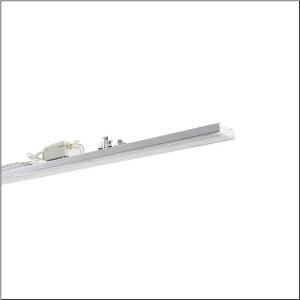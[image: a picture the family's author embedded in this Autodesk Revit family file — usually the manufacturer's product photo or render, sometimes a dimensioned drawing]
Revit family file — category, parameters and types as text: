
# Revit family: licross_11_recessed_mo_51tl107n485g
name_source: partatom
category: Lighting Fixtures
units: mm (PartAtom-declared; Revit-internal decimal feet)

## family parameters
Cut with Voids When Loaded = No
Host = Face
Light Source = No
Part Type = Normal
Room Calculation Point = No
Round Connector Dimension = Use Diameter
Shared = No

## types (1)
- Licross 11 Recessed MO (1 x LED, 8700 lm, 48.5 W, 4000K)
    Apparent Load = 49 VA
    CIE Flux Codes = 50 81 96 100 100
    Color Rendering = 80
    Color Temperature = 4000K
    Default Elevation = 1800 mm
    Description = Licross 11 Recessed MO, luminaire insert, of sheet steel, coil coated, white, length: 1.500mm, width: 66mm, height: 67mm, LED rated luminous flux: 8.710lm, light colour: 840, SDCM (Standard Deviation of Colour Matching)MacAdam ≤ 2 SDCM (initial), control gear: ON/OFF, with plug, 3-pole, with phase selection, mains connection: 220..240V, AC, 50/60Hz, rated input power: 49W, internal wiring halogen-free, primary optical cover: cover, of PMMA, light emission: direct distribution, primary light characteristic: symmetric, protection rating (complete): IP40, insulation class (complete): insulation class I (protective earthing), certification: CE, ENEC, VDE, UKCA, protection symbol: D if used in an environment without relevant dust loads with corresponding accessories, impact resistance: IK06, permissible ambient temperature for indoor applications: -35..+35°C, corresponds to IFS (International Featured Standards) requirements for safety and quality in the food industry, reducing of maximum allowable ambient temperature of 5°C with ceiling mounting, The light source and the operating device comply with the requirements of the Ecodesign Regulation (EU) 2019/2020 and are replaceable in accordance with this regulation, packaging unit: 1 piece
    Height = 58 mm
    Lamp = 1 x LED
    Lamp Light Flux = 8700 lm
    Lamp Power = 48.5 W
    Lamp count = 1
    Length = 1500 mm
    Luminous efficacy = 179 lm/W
    Manufacturer = Siteco
    ModVariant = No
    Model = 51TL107N485G
    Mounting Place = Ceiling
    Mounting Type = Pendant
    Number of Poles = 1
    OnlyDefault = Yes
    Power Factor = 1
    Product Name = Licross 11 Recessed MO
    Product group = luminaire insert | ceiling pendant
    ProductGroupID = 901
    Protection Class = Protection class I
    Protection Degree = IP 40
    RLX_Detail_Level = 1
    RLX_Emergency_Light_Flux = 0 lm
    RLX_Emergency_Type = 0
    RLX_Emergency_Type_DB = No
    RlxData = <blob elided: 20933 chars, md5=f47c12c2>
    Socket = socket
    Standby Power = 0 W
    System Light Flux = 8700 lm
    System Power = 49 W
    Type Comments = Product without accessories
    Type Image = l_1296930.jpg
    URL = http://relux.com
    VarID = ---
    Voltage = 0 V
    Weight = 0.00 kg
    Width = 66 mm

## geometry (parser evidence)
native form markers: Blend x4, Sweep x12
no freeform markers — native parametric forms only
